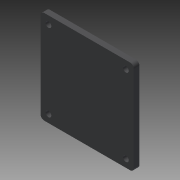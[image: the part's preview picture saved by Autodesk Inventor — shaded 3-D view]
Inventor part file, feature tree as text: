
AUTODESK INVENTOR PART (.ipt)
format: ipt  version: 2015 (Build 190159000, 159)  size: 95,232 bytes
history: native  units: mm
features: extrude x1, sketch x1
ambient origin geometry x8: Origin, YZ Plane, XZ Plane, XY Plane, X Axis, Y Axis, Z Axis, Center Point
bodies: Body1 (feature_tree)
feature tree (2):
  extrude  "Extrusion2"  Depth=2.0mm
  sketch  "Sketch3"  dims[d19=50.0mm d20=50.0mm d21=3.0mm d22=3.0mm d23=3.0mm d24=3.0mm d32=2.0mm d33=3.0mm d34=0.0mm]
